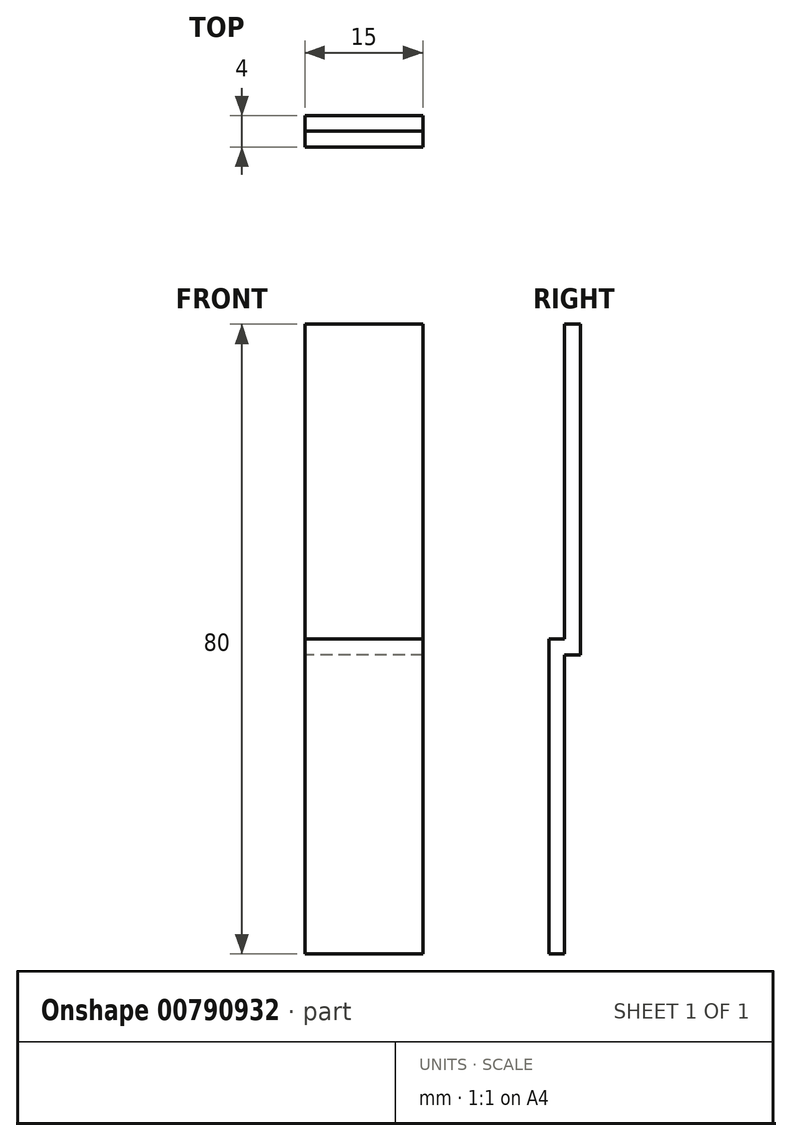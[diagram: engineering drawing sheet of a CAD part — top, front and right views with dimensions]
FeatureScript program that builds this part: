
annotation { "Feature Type Name" : "Feature", "Feature Type Description" : "" }
export const myFeature = defineFeature(function(context is Context, id is Id, definition is map)
    precondition{}
    {
        {
            var Q0;
            Q0=qCreatedBy(makeId("Right.planeOp"),FACE);
            var sketch = newSketch(context, id + "F0", { "sketchPlane" : qUnion([Q0])});
            skLineSegment(sketch, "E0", {"start": v(0, 40) * mm, "end": v(2, 40) * mm});
            skLineSegment(sketch, "E1", {"start": v(2, 40) * mm, "end": v(2, -2) * mm});
            skLineSegment(sketch, "E2", {"start": v(2, -2) * mm, "end": v(0, -2) * mm});
            skLineSegment(sketch, "E3", {"start": v(0, -2) * mm, "end": v(0, -40) * mm});
            skLineSegment(sketch, "E4", {"start": v(0, -40) * mm, "end": v(-2, -40) * mm});
            skLineSegment(sketch, "E5", {"start": v(-2, -40) * mm, "end": v(-2, 0) * mm});
            skLineSegment(sketch, "E6", {"start": v(-2, 0) * mm, "end": v(0, 0) * mm});
            skLineSegment(sketch, "E7", {"start": v(0, 0) * mm, "end": v(0, 40) * mm});
            skSolve(sketch);
        }
        {
            var Q0;
            Q0 = qSketchRegion(id + "F0", true);
            extrude(context, id + "F1", {"entities" : qUnion([Q0]), "depth" : 15 * mm, "offsetDistance" : 25 * mm});
        }
    });
